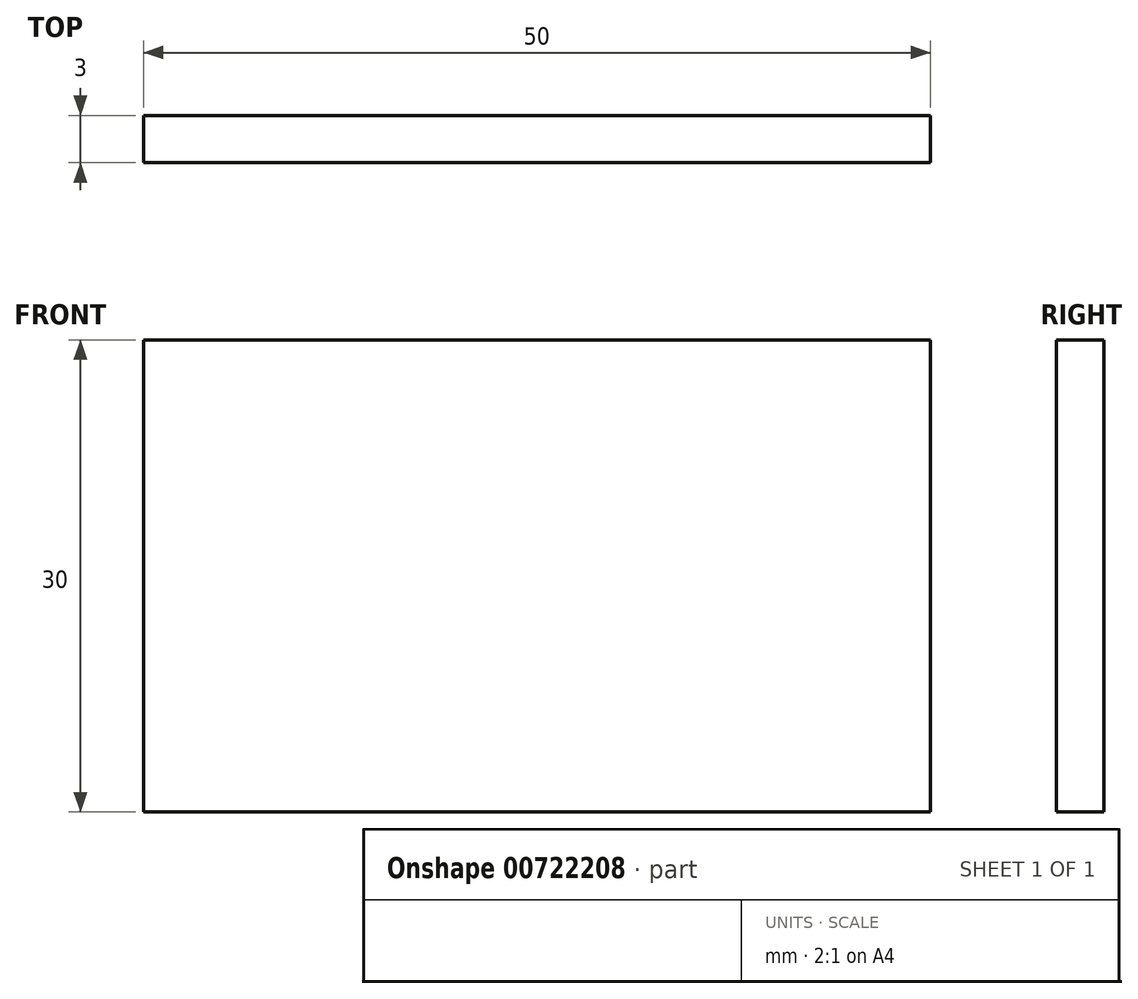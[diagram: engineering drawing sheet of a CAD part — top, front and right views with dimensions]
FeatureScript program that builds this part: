
annotation { "Feature Type Name" : "Feature", "Feature Type Description" : "" }
export const myFeature = defineFeature(function(context is Context, id is Id, definition is map)
    precondition{}
    {
        {
            var Q0;
            Q0=qCreatedBy(makeId("Front.planeOp"),FACE);
            var sketch = newSketch(context, id + "F0", { "sketchPlane" : qUnion([Q0])});
            skLineSegment(sketch, "E0", {"start": v(-50, 30) * mm, "end": v(0, 30) * mm});
            skLineSegment(sketch, "E1", {"start": v(0, 30) * mm, "end": v(0, 0) * mm});
            skLineSegment(sketch, "E2", {"start": v(0, 0) * mm, "end": v(-50, 0) * mm});
            skLineSegment(sketch, "E3", {"start": v(-50, 0) * mm, "end": v(-50, 30) * mm});
            skSolve(sketch);
        }
        {
            var Q0;
            Q0=makeQuery(id+"F0.imprint","IMPRINT",FACE,{"disambiguationData":[TD([[makeQuery(id+"F0.imprint","IMPRINT",EDGE,{"derivedFrom":sQuery(id+"F0.wireOp",EDGE,"E0")}),-1.0]])]});
            extrude(context, id + "F1", {"entities" : qUnion([Q0]), "depth" : 3 * mm, "offsetDistance" : 25 * mm});
        }
    });
